# Revit family: Lightronics_LightingFixture_WallAndCeiling_DOTT_M1
name_source: partatom
category: Lighting Fixtures
revit_build: Autodesk Revit 2016 (Build: 20160314_0715(x64)
units: mm (PartAtom-declared; Revit-internal decimal feet)

## family parameters
Cut with Voids When Loaded = No
Host = Face
Light Source = Yes
OmniClass Number = 23.80.70.00
OmniClass Title = Lighting
Part Type = Normal
Room Calculation Point = No
Round Connector Dimension = Use Diameter
Shared = No

## types (2) — shared parameters
Apparent Load = 0 VA
Assembly Code = D5020200
AssetType = Fixed
BIMObjectName = Lightronics_LightingFixture_WallAndCeiling_DOTT_M
ClassificationName = Uniclass 2015
ClassificationValue = Pr_70_70_48_85
Color = Housing: aluminium coated (DB703) or RAL 9010. Cover: UV-stabilised polycarbonate opal or frosted
Color Filter = 16777215
Default Elevation = 1219 mm
Description = Impact proof design luminaire for surface and recessed mounting
Dimming Lamp Color Temperature Shift = <None>
DocumentationLiterature = https://specifi.bimstore.co.uk
DurationUnit = 20 Years
Emit Shape Visible in Rendering = No
ExpectedLife = 10
IfcExportAs = IfcLightFixtureTypeEnum.POINTSOURCE
IfcExportType = IfcLightFixture
Keynote = V90/510
Manufacturer = Lightronics
ManufacturerName = Lightronics
Material = UV-stabilised polycarbonate
ModelReference = IP 65
NBSDescription = Surface luminaires
NBSObjectName = Lightronics -  General purpose luminaires
NBSReference = 90-60-50/405
NumberOfPoles = 1
Photometric Web File = DOTTM-LO4-1-12-350-D-F-1270-230-X-W.ies
ProductionYear = 2018
Shape = Circular
Tilt Angle = 90.00°
Type Comments = Wall and ceiling lighting – Hogro Plus. Impact proof design luminaire for surface and recessed mounting
TypeName = DOTT M
URL = https://www.lightronics.nl
Voltage = 230 V
WarrantyDurationParts = 5
WarrantyDurationUnit = Years
_BSBibleVersion = 15
_CurrentRevision = 1
_DistributedBy = www.bimstore.co.uk
zero-valued in all types: _BimSpecGuid

## per-type parameters (varying)
| type | Depth | Diameter | Emit from Circle Diameter | Height | Length | LightOffset | Model | ModelNumber | NominalDepth | NominalHeight | NominalLength | Recessed | Size | SurfaceMounted |
| Surface Mounted | 360 mm  [stored 1.1811 ft] | 360 mm  [stored 1.1811 ft] | 360 mm  [stored 1.1811 ft] | 105 mm  [stored 0.344488 ft] | 360 mm  [stored 1.1811 ft] | 45 mm  [stored 0.147638 ft] | DOTT M - Surface Mounted | DOTT M - Surface Mounted | 360 mm  [stored 1.1811 ft] | 105 mm  [stored 0.344488 ft] | 360 mm  [stored 1.1811 ft] | No | 360x105 | Yes |
| Recessed | 445 mm  [stored 1.45997 ft] | 445 mm  [stored 1.45997 ft] | 400 mm  [stored 1.31234 ft] | 124 mm  [stored 0.406824 ft] | 445 mm  [stored 1.45997 ft] | 15 mm  [stored 0.0492126 ft] | DOTT M - Recessed Mounted | DOTT M - Recessed Mounted | 445 mm  [stored 1.45997 ft] | 124 mm  [stored 0.406824 ft] | 445 mm  [stored 1.45997 ft] | Yes | 445x124 | No |

note: [stored X ft] marks values corroborated as IEEE doubles in the binary element streams (Revit-internal decimal feet)

## geometry (parser evidence)
native form markers: Sweep x3
no freeform markers — native parametric forms only
